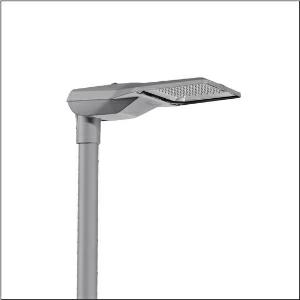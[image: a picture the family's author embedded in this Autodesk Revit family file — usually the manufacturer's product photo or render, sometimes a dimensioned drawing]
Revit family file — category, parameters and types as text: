
# Revit family: streetlight_sl_21_midi___pc-l_5xe3f43s08mb_b5db
name_source: partatom
category: Lighting Fixtures
units: mm (PartAtom-declared; Revit-internal decimal feet)

## family parameters
Cut with Voids When Loaded = No
Host = Face
Light Source = No
Part Type = Normal
Room Calculation Point = No
Round Connector Dimension = Use Diameter
Shared = No

## types (1)
- --- (1 x LED, 19200 lm, 147 W, 4000K)
    Apparent Load = 147 VA
    CIE Flux Codes = 38 78 98 100 100
    Color Rendering = 70
    Color Temperature = 4000K
    Default Elevation = 1800 mm
    Description = Streetlight SL 21 midi, mast luminaire, primary light control with lens, of PMMA, primary optical cover: cover, of toughened safety glass, transparent, light distribution: PC-L, light emission: direct distribution, primary light characteristic: asymmetric, left, installation type: side-entry, post-top, LED, High Power LED, rated luminous flux: 19.200lm, luminous efficacy: 131lm/W, light colour: 740, colour temperature: 4000K, control: overheat protection, constant luminous flux control, time-dependent luminous flux control, flexible luminous flux parameterisation, presetting dimming logarithmic, mains connection: 230..240V, AC, 50/60Hz, start of lifetime: 147W, end of service life: 155W, reduction: 65W, luminaire housing, of diecast aluminium, powder-coated, Siteco® metallic grey (DB 702S), corrosivity category C5 mid according to DIN EN ISO 12944, please order mast flange separately, inclination adjustable: 0°, 5°, 10°, 15°, sealing non-destructively replaceable, multi-level sealing system, length: 644mm, width: 335mm, height: 110mm, mast flange for spigot size: 42mm (side-entry): 5XC10008XM4, 60/48mm (side-entry/post-top): 5XC10108XM2, 76/60mm (side-entry/post-top): 5XC10108XM1, Smart Interface above, protection rating (complete): IP66, insulation class (complete): insulation class II (safety insulation), certification: CE, ENEC, ENEC+, VDE, impact resistance: IK09, permissible operating ambient temperature for outdoor applications: -40..+50°C, standard-compliant lighting for roads and squares, packaging unit: 1 piece

Light Distribution: PC-L
    Height = 111 mm
    Lamp = 1 x LED
    Lamp Light Flux = 19200 lm
    Lamp Power = 147 W
    Lamp count = 1
    Length = 644 mm
    Luminous efficacy = 131 lm/W
    Manufacturer = Siteco
    ModVariant = No
    Model = 5XE3F43S08MB
    Number of Poles = 1
    OnlyDefault = Yes
    Power Factor = 1
    Product Name = Streetlight SL 21 midi | PC-L
    Product group = mast luminaire | pylon top
    ProductGroupID = 6100
    Protection Class = Protection class II
    Protection Degree = IP 66
    RLX_Detail_Level = 1
    RLX_Emergency_Light_Flux = 0 lm
    RLX_Emergency_Type = 0
    RLX_Emergency_Type_DB = No
    RlxData = <blob elided: 93065 chars, md5=9ba4689c>
    Socket = socket
    Standby Power = 0 W
    System Light Flux = 19200 lm
    System Power = 147 W
    Type Comments = factory setting: luminous flux: 100 % | dim-lin: 254 | 750 mA
    Type Image = l_1004302.jpg
    URL = http://relux.com
    VarID = @adj_023065
    Voltage = 0 V
    Weight = 0.00 kg
    Width = 336 mm

## geometry (parser evidence)
native form markers: Blend x4, Sweep x11
no freeform markers — native parametric forms only
